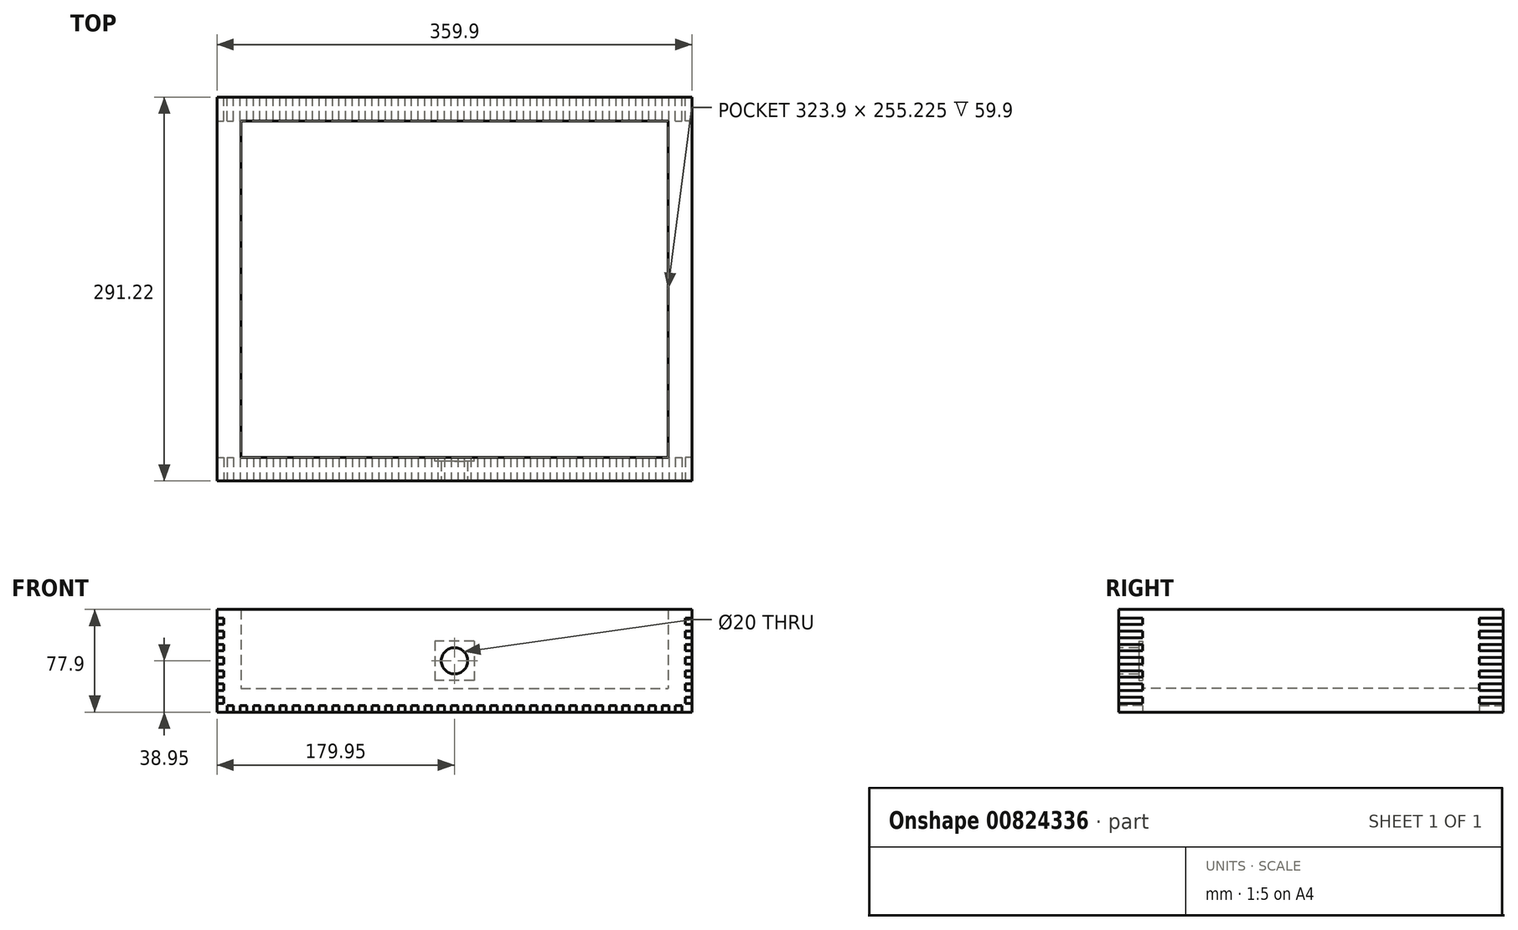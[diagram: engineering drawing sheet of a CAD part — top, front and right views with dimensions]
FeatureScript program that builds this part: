
annotation { "Feature Type Name" : "Feature", "Feature Type Description" : "" }
export const myFeature = defineFeature(function(context is Context, id is Id, definition is map)
    precondition{}
    {
        {
            var Q0;
            Q0=qCreatedBy(makeId("Top.planeOp"),FACE);
            var sketch = newSketch(context, id + "F0", { "sketchPlane" : qUnion([Q0])});
            skLineSegment(sketch, "E0.bottom", {"start": v(-179.95, 145.61) * mm, "end": v(179.95, 145.61) * mm});
            skLineSegment(sketch, "E0.top", {"start": v(-179.95, -145.61) * mm, "end": v(179.95, -145.61) * mm});
            skLineSegment(sketch, "E0.left", {"start": v(-179.95, 145.61) * mm, "end": v(-179.95, -145.61) * mm});
            skLineSegment(sketch, "E0.right", {"start": v(179.95, 145.61) * mm, "end": v(179.95, -145.61) * mm});
            skPoint(sketch, "E0.middle", {"position": v(0, 0) * mm});
            skSolve(sketch);
        }
        {
            var Q0;
            Q0 = qSketchRegion(id + "F0", true);
            extrude(context, id + "F1", {"entities" : qUnion([Q0]), "depth" : 18 * mm, "offsetDistance" : 25 * mm});
        }
        {
            var Q0;
            Q0=makeQuery(id+"F1.opExtrude","CAP_FACE",FACE,{"disambiguationData":[OSD([sQuery(id+"F0.wireOp",EDGE,"E0.bottom"),sQuery(id+"F0.wireOp",EDGE,"E0.top"),sQuery(id+"F0.wireOp",EDGE,"E0.left"),sQuery(id+"F0.wireOp",EDGE,"E0.right")])],"isStart":false});
            var sketch = newSketch(context, id + "F2", { "sketchPlane" : qUnion([Q0])});
            skLineSegment(sketch, "E1.bottom", {"start": v(-179.95, -145.61) * mm, "end": v(179.95, -145.61) * mm});
            skLineSegment(sketch, "E1.top", {"start": v(-179.95, -127.61) * mm, "end": v(179.95, -127.61) * mm});
            skLineSegment(sketch, "E1.left", {"start": v(-179.95, -145.61) * mm, "end": v(-179.95, -127.61) * mm});
            skLineSegment(sketch, "E1.right", {"start": v(179.95, -145.61) * mm, "end": v(179.95, -127.61) * mm});
            skLineSegment(sketch, "E2.MirrorCS", {"start": v(-179.95, 127.61) * mm, "end": v(179.95, 127.61) * mm});
            skLineSegment(sketch, "E3.MirrorCS", {"start": v(-179.95, 145.61) * mm, "end": v(179.95, 145.61) * mm});
            skLineSegment(sketch, "E4.MirrorCS", {"start": v(179.95, 145.61) * mm, "end": v(179.95, 127.61) * mm});
            skLineSegment(sketch, "E5.MirrorCS", {"start": v(-179.95, 145.61) * mm, "end": v(-179.95, 127.61) * mm});
            skSolve(sketch);
        }
        {
            var Q0;
            Q0 = qSketchRegion(id + "F2", true);
            extrude(context, id + "F3", {"entities" : qUnion([Q0]), "operationType" : NewBodyOperationType.ADD, "depth" : 59.9 * mm, "offsetDistance" : 25 * mm});
        }
        {
            var Q0;
            Q0=makeQuery(id+"F1.opExtrude","CAP_FACE",FACE,{"disambiguationData":[OSD([sQuery(id+"F0.wireOp",EDGE,"E0.bottom"),sQuery(id+"F0.wireOp",EDGE,"E0.top"),sQuery(id+"F0.wireOp",EDGE,"E0.left"),sQuery(id+"F0.wireOp",EDGE,"E0.right")])],"isStart":false});
            var sketch = newSketch(context, id + "F4", { "sketchPlane" : qUnion([Q0])});
            skLineSegment(sketch, "E6.bottom", {"start": v(179.95, 127.61) * mm, "end": v(161.95, 127.61) * mm});
            skLineSegment(sketch, "E6.top", {"start": v(179.95, -127.61) * mm, "end": v(161.95, -127.61) * mm});
            skLineSegment(sketch, "E6.left", {"start": v(179.95, 127.61) * mm, "end": v(179.95, -127.61) * mm});
            skLineSegment(sketch, "E6.right", {"start": v(161.95, 127.61) * mm, "end": v(161.95, -127.61) * mm});
            skLineSegment(sketch, "E7.MirrorCS", {"start": v(-179.95, 127.61) * mm, "end": v(-161.95, 127.61) * mm});
            skLineSegment(sketch, "E8.MirrorCS", {"start": v(-179.95, -127.61) * mm, "end": v(-161.95, -127.61) * mm});
            skLineSegment(sketch, "E9.MirrorCS", {"start": v(-179.95, 127.61) * mm, "end": v(-179.95, -127.61) * mm});
            skLineSegment(sketch, "E10.MirrorCS", {"start": v(-161.95, 127.61) * mm, "end": v(-161.95, -127.61) * mm});
            skSolve(sketch);
        }
        {
            var Q0;
            Q0 = qSketchRegion(id + "F4", true);
            extrude(context, id + "F5", {"entities" : qUnion([Q0]), "operationType" : NewBodyOperationType.ADD, "depth" : 59.9 * mm, "offsetDistance" : 25 * mm});
        }
        {
            var Q0;
            Q0=makeQuery(id+"F3.boolean.opBoolean","MERGE",FACE,{"derivedFrom":[makeQuery(id+"F1.opExtrude","SWEPT_FACE",FACE,{"disambiguationData":[OSD([sQuery(id+"F0.wireOp",EDGE,"E0.top")])]}),makeQuery(id+"F3.opExtrude","SWEPT_FACE",FACE,{"disambiguationData":[OSD([sQuery(id+"F2.wireOp",EDGE,"E1.bottom")])]})]});
            var sketch = newSketch(context, id + "F6", { "sketchPlane" : qUnion([Q0])});
            skLineSegment(sketch, "E11", {"start": v(0, 0) * mm, "end": v(0, 74.36) * mm, "construction": true});
            skLineSegment(sketch, "E12", {"start": v(-179.95, 38.95) * mm, "end": v(179.95, 38.95) * mm, "construction": true});
            skLineSegment(sketch, "E13.bottom", {"start": v(-179.95, 41.45) * mm, "end": v(-174.95, 41.45) * mm});
            skLineSegment(sketch, "E13.top", {"start": v(-179.95, 36.45) * mm, "end": v(-174.95, 36.45) * mm});
            skLineSegment(sketch, "E13.left", {"start": v(-179.95, 41.45) * mm, "end": v(-179.95, 36.45) * mm});
            skLineSegment(sketch, "E13.right", {"start": v(-174.95, 41.45) * mm, "end": v(-174.95, 36.45) * mm});
            skPoint(sketch, "E13.middle", {"position": v(-177.45, 38.95) * mm});
            skLineSegment(sketch, "E14.0.1.0", {"start": v(-179.95, 51.45) * mm, "end": v(-179.95, 46.45) * mm});
            skLineSegment(sketch, "E14.0.1.1", {"start": v(-174.95, 51.45) * mm, "end": v(-174.95, 46.45) * mm});
            skLineSegment(sketch, "E14.0.1.2", {"start": v(-179.95, 51.45) * mm, "end": v(-174.95, 51.45) * mm});
            skPoint(sketch, "E14.0.1.3", {"position": v(-177.45, 48.95) * mm});
            skLineSegment(sketch, "E14.0.1.4", {"start": v(-179.95, 46.45) * mm, "end": v(-174.95, 46.45) * mm});
            skLineSegment(sketch, "E14.0.2.0", {"start": v(-179.95, 61.45) * mm, "end": v(-179.95, 56.45) * mm});
            skLineSegment(sketch, "E14.0.2.1", {"start": v(-174.95, 61.45) * mm, "end": v(-174.95, 56.45) * mm});
            skLineSegment(sketch, "E14.0.2.2", {"start": v(-179.95, 61.45) * mm, "end": v(-174.95, 61.45) * mm});
            skPoint(sketch, "E14.0.2.3", {"position": v(-177.45, 58.95) * mm});
            skLineSegment(sketch, "E14.0.2.4", {"start": v(-179.95, 56.45) * mm, "end": v(-174.95, 56.45) * mm});
            skLineSegment(sketch, "E14.0.3.0", {"start": v(-179.95, 71.45) * mm, "end": v(-179.95, 66.45) * mm});
            skLineSegment(sketch, "E14.0.3.1", {"start": v(-174.95, 71.45) * mm, "end": v(-174.95, 66.45) * mm});
            skLineSegment(sketch, "E14.0.3.2", {"start": v(-179.95, 71.45) * mm, "end": v(-174.95, 71.45) * mm});
            skPoint(sketch, "E14.0.3.3", {"position": v(-177.45, 68.95) * mm});
            skLineSegment(sketch, "E14.0.3.4", {"start": v(-179.95, 66.45) * mm, "end": v(-174.95, 66.45) * mm});
            skLineSegment(sketch, "E14.direction1", {"start": v(-179.95, 36.45) * mm, "end": v(-154.95, 36.45) * mm, "construction": true});
            skLineSegment(sketch, "E14.direction2", {"start": v(-179.95, 36.45) * mm, "end": v(-179.95, 46.45) * mm, "construction": true});
            skLineSegment(sketch, "E15.MirrorCS", {"start": v(-179.95, 36.45) * mm, "end": v(-179.95, 41.45) * mm});
            skLineSegment(sketch, "E16.MirrorCS", {"start": v(-179.95, 21.45) * mm, "end": v(-174.95, 21.45) * mm});
            skPoint(sketch, "E17.MirrorP", {"position": v(-177.45, 28.95) * mm});
            skLineSegment(sketch, "E18.MirrorCS", {"start": v(-179.95, 6.45) * mm, "end": v(-174.95, 6.45) * mm});
            skLineSegment(sketch, "E19.MirrorCS", {"start": v(-174.95, 6.45) * mm, "end": v(-174.95, 11.45) * mm});
            skLineSegment(sketch, "E20.MirrorCS", {"start": v(-174.95, 16.45) * mm, "end": v(-174.95, 21.45) * mm});
            skLineSegment(sketch, "E21.MirrorCS", {"start": v(-174.95, 36.45) * mm, "end": v(-174.95, 41.45) * mm});
            skPoint(sketch, "E22.MirrorP", {"position": v(-177.45, 8.95) * mm});
            skLineSegment(sketch, "E23.MirrorCS", {"start": v(-179.95, 16.45) * mm, "end": v(-179.95, 21.45) * mm});
            skPoint(sketch, "E24.MirrorP", {"position": v(-177.45, 18.95) * mm});
            skLineSegment(sketch, "E25.MirrorCS", {"start": v(-179.95, 11.45) * mm, "end": v(-174.95, 11.45) * mm});
            skLineSegment(sketch, "E26.MirrorCS", {"start": v(-174.95, 26.45) * mm, "end": v(-174.95, 31.45) * mm});
            skLineSegment(sketch, "E27.MirrorCS", {"start": v(-179.95, 26.45) * mm, "end": v(-174.95, 26.45) * mm});
            skLineSegment(sketch, "E28.MirrorCS", {"start": v(-179.95, 6.45) * mm, "end": v(-179.95, 11.45) * mm});
            skLineSegment(sketch, "E29.MirrorCS", {"start": v(-179.95, 41.45) * mm, "end": v(-179.95, 31.45) * mm, "construction": true});
            skLineSegment(sketch, "E30.MirrorCS", {"start": v(-179.95, 31.45) * mm, "end": v(-174.95, 31.45) * mm});
            skLineSegment(sketch, "E31.MirrorCS", {"start": v(-179.95, 16.45) * mm, "end": v(-174.95, 16.45) * mm});
            skLineSegment(sketch, "E32.MirrorCS", {"start": v(-179.95, 26.45) * mm, "end": v(-179.95, 31.45) * mm});
            skLineSegment(sketch, "E33.MirrorCS", {"start": v(179.95, 41.45) * mm, "end": v(179.95, 36.45) * mm});
            skLineSegment(sketch, "E34.MirrorCS", {"start": v(179.95, 36.45) * mm, "end": v(179.95, 41.45) * mm});
            skPoint(sketch, "E35.MirrorP", {"position": v(177.45, 28.95) * mm});
            skLineSegment(sketch, "E36.MirrorCS", {"start": v(179.95, 31.45) * mm, "end": v(174.95, 31.45) * mm});
            skLineSegment(sketch, "E37.MirrorCS", {"start": v(179.95, 26.45) * mm, "end": v(179.95, 31.45) * mm});
            skPoint(sketch, "E38.MirrorP", {"position": v(177.45, 38.95) * mm});
            skLineSegment(sketch, "E39.MirrorCS", {"start": v(174.95, 26.45) * mm, "end": v(174.95, 31.45) * mm});
            skLineSegment(sketch, "E40.MirrorCS", {"start": v(179.95, 36.45) * mm, "end": v(174.95, 36.45) * mm});
            skLineSegment(sketch, "E41.MirrorCS", {"start": v(174.95, 41.45) * mm, "end": v(174.95, 36.45) * mm});
            skLineSegment(sketch, "E42.MirrorCS", {"start": v(179.95, 41.45) * mm, "end": v(174.95, 41.45) * mm});
            skLineSegment(sketch, "E43.MirrorCS", {"start": v(179.95, 26.45) * mm, "end": v(174.95, 26.45) * mm});
            skLineSegment(sketch, "E44.MirrorCS", {"start": v(179.95, 16.45) * mm, "end": v(179.95, 21.45) * mm});
            skLineSegment(sketch, "E45.MirrorCS", {"start": v(179.95, 66.45) * mm, "end": v(174.95, 66.45) * mm});
            skLineSegment(sketch, "E46.MirrorCS", {"start": v(174.95, 61.45) * mm, "end": v(174.95, 56.45) * mm});
            skPoint(sketch, "E47.MirrorP", {"position": v(177.45, 8.95) * mm});
            skPoint(sketch, "E48.MirrorP", {"position": v(177.45, 58.95) * mm});
            skLineSegment(sketch, "E49.MirrorCS", {"start": v(174.95, 51.45) * mm, "end": v(174.95, 46.45) * mm});
            skLineSegment(sketch, "E50.MirrorCS", {"start": v(179.95, 61.45) * mm, "end": v(179.95, 56.45) * mm});
            skLineSegment(sketch, "E51.MirrorCS", {"start": v(179.95, 61.45) * mm, "end": v(174.95, 61.45) * mm});
            skLineSegment(sketch, "E52.MirrorCS", {"start": v(179.95, 41.45) * mm, "end": v(179.95, 31.45) * mm, "construction": true});
            skLineSegment(sketch, "E53.MirrorCS", {"start": v(179.95, 36.45) * mm, "end": v(179.95, 46.45) * mm, "construction": true});
            skPoint(sketch, "E54.MirrorP", {"position": v(177.45, 48.95) * mm});
            skPoint(sketch, "E55.MirrorP", {"position": v(177.45, 68.95) * mm});
            skLineSegment(sketch, "E56.MirrorCS", {"start": v(179.95, 51.45) * mm, "end": v(174.95, 51.45) * mm});
            skLineSegment(sketch, "E57.MirrorCS", {"start": v(179.95, 71.45) * mm, "end": v(174.95, 71.45) * mm});
            skLineSegment(sketch, "E58.MirrorCS", {"start": v(179.95, 16.45) * mm, "end": v(174.95, 16.45) * mm});
            skLineSegment(sketch, "E59.MirrorCS", {"start": v(179.95, 46.45) * mm, "end": v(174.95, 46.45) * mm});
            skPoint(sketch, "E60.MirrorP", {"position": v(177.45, 18.95) * mm});
            skLineSegment(sketch, "E61.MirrorCS", {"start": v(174.95, 6.45) * mm, "end": v(174.95, 11.45) * mm});
            skLineSegment(sketch, "E62.MirrorCS", {"start": v(179.95, 51.45) * mm, "end": v(179.95, 46.45) * mm});
            skLineSegment(sketch, "E63.MirrorCS", {"start": v(179.95, 21.45) * mm, "end": v(174.95, 21.45) * mm});
            skLineSegment(sketch, "E64.MirrorCS", {"start": v(179.95, 56.45) * mm, "end": v(174.95, 56.45) * mm});
            skLineSegment(sketch, "E65.MirrorCS", {"start": v(179.95, 6.45) * mm, "end": v(179.95, 11.45) * mm});
            skLineSegment(sketch, "E66.MirrorCS", {"start": v(179.95, 71.45) * mm, "end": v(179.95, 66.45) * mm});
            skLineSegment(sketch, "E67.MirrorCS", {"start": v(174.95, 36.45) * mm, "end": v(174.95, 41.45) * mm});
            skLineSegment(sketch, "E68.MirrorCS", {"start": v(174.95, 16.45) * mm, "end": v(174.95, 21.45) * mm});
            skLineSegment(sketch, "E69.MirrorCS", {"start": v(179.95, 6.45) * mm, "end": v(174.95, 6.45) * mm});
            skLineSegment(sketch, "E70.MirrorCS", {"start": v(174.95, 71.45) * mm, "end": v(174.95, 66.45) * mm});
            skLineSegment(sketch, "E71.MirrorCS", {"start": v(179.95, 11.45) * mm, "end": v(174.95, 11.45) * mm});
            skLineSegment(sketch, "E72.bottom", {"start": v(-2.5, 5) * mm, "end": v(2.5, 5) * mm});
            skLineSegment(sketch, "E72.top", {"start": v(-2.5, 0) * mm, "end": v(2.5, 0) * mm});
            skLineSegment(sketch, "E72.left", {"start": v(-2.5, 5) * mm, "end": v(-2.5, 0) * mm});
            skLineSegment(sketch, "E72.right", {"start": v(2.5, 5) * mm, "end": v(2.5, 0) * mm});
            skPoint(sketch, "E72.middle", {"position": v(0, 2.5) * mm});
            skLineSegment(sketch, "E73.1.0.0", {"start": v(7.5, 5) * mm, "end": v(7.5, 0) * mm});
            skLineSegment(sketch, "E73.1.0.1", {"start": v(7.5, 5) * mm, "end": v(12.5, 5) * mm});
            skLineSegment(sketch, "E73.1.0.2", {"start": v(12.5, 5) * mm, "end": v(12.5, 0) * mm});
            skPoint(sketch, "E73.1.0.3", {"position": v(10, 2.5) * mm});
            skLineSegment(sketch, "E73.1.0.4", {"start": v(7.5, 0) * mm, "end": v(12.5, 0) * mm});
            skLineSegment(sketch, "E73.2.0.0", {"start": v(17.5, 5) * mm, "end": v(17.5, 0) * mm});
            skLineSegment(sketch, "E73.2.0.1", {"start": v(17.5, 5) * mm, "end": v(22.5, 5) * mm});
            skLineSegment(sketch, "E73.2.0.2", {"start": v(22.5, 5) * mm, "end": v(22.5, 0) * mm});
            skPoint(sketch, "E73.2.0.3", {"position": v(20, 2.5) * mm});
            skLineSegment(sketch, "E73.2.0.4", {"start": v(17.5, 0) * mm, "end": v(22.5, 0) * mm});
            skLineSegment(sketch, "E73.3.0.0", {"start": v(27.5, 5) * mm, "end": v(27.5, 0) * mm});
            skLineSegment(sketch, "E73.3.0.1", {"start": v(27.5, 5) * mm, "end": v(32.5, 5) * mm});
            skLineSegment(sketch, "E73.3.0.2", {"start": v(32.5, 5) * mm, "end": v(32.5, 0) * mm});
            skPoint(sketch, "E73.3.0.3", {"position": v(30, 2.5) * mm});
            skLineSegment(sketch, "E73.3.0.4", {"start": v(27.5, 0) * mm, "end": v(32.5, 0) * mm});
            skLineSegment(sketch, "E73.4.0.0", {"start": v(37.5, 5) * mm, "end": v(37.5, 0) * mm});
            skLineSegment(sketch, "E73.4.0.1", {"start": v(37.5, 5) * mm, "end": v(42.5, 5) * mm});
            skLineSegment(sketch, "E73.4.0.2", {"start": v(42.5, 5) * mm, "end": v(42.5, 0) * mm});
            skPoint(sketch, "E73.4.0.3", {"position": v(40, 2.5) * mm});
            skLineSegment(sketch, "E73.4.0.4", {"start": v(37.5, 0) * mm, "end": v(42.5, 0) * mm});
            skLineSegment(sketch, "E73.5.0.0", {"start": v(47.5, 5) * mm, "end": v(47.5, 0) * mm});
            skLineSegment(sketch, "E73.5.0.1", {"start": v(47.5, 5) * mm, "end": v(52.5, 5) * mm});
            skLineSegment(sketch, "E73.5.0.2", {"start": v(52.5, 5) * mm, "end": v(52.5, 0) * mm});
            skPoint(sketch, "E73.5.0.3", {"position": v(50, 2.5) * mm});
            skLineSegment(sketch, "E73.5.0.4", {"start": v(47.5, 0) * mm, "end": v(52.5, 0) * mm});
            skLineSegment(sketch, "E73.6.0.0", {"start": v(57.5, 5) * mm, "end": v(57.5, 0) * mm});
            skLineSegment(sketch, "E73.6.0.1", {"start": v(57.5, 5) * mm, "end": v(62.5, 5) * mm});
            skLineSegment(sketch, "E73.6.0.2", {"start": v(62.5, 5) * mm, "end": v(62.5, 0) * mm});
            skPoint(sketch, "E73.6.0.3", {"position": v(60, 2.5) * mm});
            skLineSegment(sketch, "E73.6.0.4", {"start": v(57.5, 0) * mm, "end": v(62.5, 0) * mm});
            skLineSegment(sketch, "E73.7.0.0", {"start": v(67.5, 5) * mm, "end": v(67.5, 0) * mm});
            skLineSegment(sketch, "E73.7.0.1", {"start": v(67.5, 5) * mm, "end": v(72.5, 5) * mm});
            skLineSegment(sketch, "E73.7.0.2", {"start": v(72.5, 5) * mm, "end": v(72.5, 0) * mm});
            skPoint(sketch, "E73.7.0.3", {"position": v(70, 2.5) * mm});
            skLineSegment(sketch, "E73.7.0.4", {"start": v(67.5, 0) * mm, "end": v(72.5, 0) * mm});
            skLineSegment(sketch, "E73.8.0.0", {"start": v(77.5, 5) * mm, "end": v(77.5, 0) * mm});
            skLineSegment(sketch, "E73.8.0.1", {"start": v(77.5, 5) * mm, "end": v(82.5, 5) * mm});
            skLineSegment(sketch, "E73.8.0.2", {"start": v(82.5, 5) * mm, "end": v(82.5, 0) * mm});
            skPoint(sketch, "E73.8.0.3", {"position": v(80, 2.5) * mm});
            skLineSegment(sketch, "E73.8.0.4", {"start": v(77.5, 0) * mm, "end": v(82.5, 0) * mm});
            skLineSegment(sketch, "E73.9.0.0", {"start": v(87.5, 5) * mm, "end": v(87.5, 0) * mm});
            skLineSegment(sketch, "E73.9.0.1", {"start": v(87.5, 5) * mm, "end": v(92.5, 5) * mm});
            skLineSegment(sketch, "E73.9.0.2", {"start": v(92.5, 5) * mm, "end": v(92.5, 0) * mm});
            skPoint(sketch, "E73.9.0.3", {"position": v(90, 2.5) * mm});
            skLineSegment(sketch, "E73.9.0.4", {"start": v(87.5, 0) * mm, "end": v(92.5, 0) * mm});
            skLineSegment(sketch, "E73.10.0.0", {"start": v(97.5, 5) * mm, "end": v(97.5, 0) * mm});
            skLineSegment(sketch, "E73.10.0.1", {"start": v(97.5, 5) * mm, "end": v(102.5, 5) * mm});
            skLineSegment(sketch, "E73.10.0.2", {"start": v(102.5, 5) * mm, "end": v(102.5, 0) * mm});
            skPoint(sketch, "E73.10.0.3", {"position": v(100, 2.5) * mm});
            skLineSegment(sketch, "E73.10.0.4", {"start": v(97.5, 0) * mm, "end": v(102.5, 0) * mm});
            skLineSegment(sketch, "E73.11.0.0", {"start": v(107.5, 5) * mm, "end": v(107.5, 0) * mm});
            skLineSegment(sketch, "E73.11.0.1", {"start": v(107.5, 5) * mm, "end": v(112.5, 5) * mm});
            skLineSegment(sketch, "E73.11.0.2", {"start": v(112.5, 5) * mm, "end": v(112.5, 0) * mm});
            skPoint(sketch, "E73.11.0.3", {"position": v(110, 2.5) * mm});
            skLineSegment(sketch, "E73.11.0.4", {"start": v(107.5, 0) * mm, "end": v(112.5, 0) * mm});
            skLineSegment(sketch, "E73.12.0.0", {"start": v(117.5, 5) * mm, "end": v(117.5, 0) * mm});
            skLineSegment(sketch, "E73.12.0.1", {"start": v(117.5, 5) * mm, "end": v(122.5, 5) * mm});
            skLineSegment(sketch, "E73.12.0.2", {"start": v(122.5, 5) * mm, "end": v(122.5, 0) * mm});
            skPoint(sketch, "E73.12.0.3", {"position": v(120, 2.5) * mm});
            skLineSegment(sketch, "E73.12.0.4", {"start": v(117.5, 0) * mm, "end": v(122.5, 0) * mm});
            skLineSegment(sketch, "E73.13.0.0", {"start": v(127.5, 5) * mm, "end": v(127.5, 0) * mm});
            skLineSegment(sketch, "E73.13.0.1", {"start": v(127.5, 5) * mm, "end": v(132.5, 5) * mm});
            skLineSegment(sketch, "E73.13.0.2", {"start": v(132.5, 5) * mm, "end": v(132.5, 0) * mm});
            skPoint(sketch, "E73.13.0.3", {"position": v(130, 2.5) * mm});
            skLineSegment(sketch, "E73.13.0.4", {"start": v(127.5, 0) * mm, "end": v(132.5, 0) * mm});
            skLineSegment(sketch, "E73.14.0.0", {"start": v(137.5, 5) * mm, "end": v(137.5, 0) * mm});
            skLineSegment(sketch, "E73.14.0.1", {"start": v(137.5, 5) * mm, "end": v(142.5, 5) * mm});
            skLineSegment(sketch, "E73.14.0.2", {"start": v(142.5, 5) * mm, "end": v(142.5, 0) * mm});
            skPoint(sketch, "E73.14.0.3", {"position": v(140, 2.5) * mm});
            skLineSegment(sketch, "E73.14.0.4", {"start": v(137.5, 0) * mm, "end": v(142.5, 0) * mm});
            skLineSegment(sketch, "E73.15.0.0", {"start": v(147.5, 5) * mm, "end": v(147.5, 0) * mm});
            skLineSegment(sketch, "E73.15.0.1", {"start": v(147.5, 5) * mm, "end": v(152.5, 5) * mm});
            skLineSegment(sketch, "E73.15.0.2", {"start": v(152.5, 5) * mm, "end": v(152.5, 0) * mm});
            skPoint(sketch, "E73.15.0.3", {"position": v(150, 2.5) * mm});
            skLineSegment(sketch, "E73.15.0.4", {"start": v(147.5, 0) * mm, "end": v(152.5, 0) * mm});
            skLineSegment(sketch, "E73.16.0.0", {"start": v(157.5, 5) * mm, "end": v(157.5, 0) * mm});
            skLineSegment(sketch, "E73.16.0.1", {"start": v(157.5, 5) * mm, "end": v(162.5, 5) * mm});
            skLineSegment(sketch, "E73.16.0.2", {"start": v(162.5, 5) * mm, "end": v(162.5, 0) * mm});
            skPoint(sketch, "E73.16.0.3", {"position": v(160, 2.5) * mm});
            skLineSegment(sketch, "E73.16.0.4", {"start": v(157.5, 0) * mm, "end": v(162.5, 0) * mm});
            skLineSegment(sketch, "E73.17.0.0", {"start": v(167.5, 5) * mm, "end": v(167.5, 0) * mm});
            skLineSegment(sketch, "E73.17.0.1", {"start": v(167.5, 5) * mm, "end": v(172.5, 5) * mm});
            skLineSegment(sketch, "E73.17.0.2", {"start": v(172.5, 5) * mm, "end": v(172.5, 0) * mm});
            skPoint(sketch, "E73.17.0.3", {"position": v(170, 2.5) * mm});
            skLineSegment(sketch, "E73.17.0.4", {"start": v(167.5, 0) * mm, "end": v(172.5, 0) * mm});
            skLineSegment(sketch, "E73.direction1", {"start": v(-2.5, 0) * mm, "end": v(7.5, 0) * mm, "construction": true});
            skLineSegment(sketch, "E74.MirrorCS", {"start": v(2.5, 0) * mm, "end": v(-7.5, 0) * mm, "construction": true});
            skLineSegment(sketch, "E75.MirrorCS", {"start": v(-157.5, 5) * mm, "end": v(-162.5, 5) * mm});
            skLineSegment(sketch, "E76.MirrorCS", {"start": v(-92.5, 5) * mm, "end": v(-92.5, 0) * mm});
            skLineSegment(sketch, "E77.MirrorCS", {"start": v(-132.5, 5) * mm, "end": v(-132.5, 0) * mm});
            skLineSegment(sketch, "E78.MirrorCS", {"start": v(-147.5, 5) * mm, "end": v(-152.5, 5) * mm});
            skLineSegment(sketch, "E79.MirrorCS", {"start": v(-82.5, 5) * mm, "end": v(-82.5, 0) * mm});
            skLineSegment(sketch, "E80.MirrorCS", {"start": v(-137.5, 5) * mm, "end": v(-142.5, 5) * mm});
            skLineSegment(sketch, "E81.MirrorCS", {"start": v(-87.5, 5) * mm, "end": v(-92.5, 5) * mm});
            skLineSegment(sketch, "E82.MirrorCS", {"start": v(-67.5, 5) * mm, "end": v(-67.5, 0) * mm});
            skLineSegment(sketch, "E83.MirrorCS", {"start": v(-167.5, 5) * mm, "end": v(-172.5, 5) * mm});
            skLineSegment(sketch, "E84.MirrorCS", {"start": v(-37.5, 5) * mm, "end": v(-37.5, 0) * mm});
            skLineSegment(sketch, "E85.MirrorCS", {"start": v(-87.5, 0) * mm, "end": v(-92.5, 0) * mm});
            skLineSegment(sketch, "E86.MirrorCS", {"start": v(-117.5, 5) * mm, "end": v(-122.5, 5) * mm});
            skLineSegment(sketch, "E87.MirrorCS", {"start": v(-172.5, 5) * mm, "end": v(-172.5, 0) * mm});
            skLineSegment(sketch, "E88.MirrorCS", {"start": v(-152.5, 5) * mm, "end": v(-152.5, 0) * mm});
            skLineSegment(sketch, "E89.MirrorCS", {"start": v(-67.5, 5) * mm, "end": v(-72.5, 5) * mm});
            skLineSegment(sketch, "E90.MirrorCS", {"start": v(-62.5, 5) * mm, "end": v(-62.5, 0) * mm});
            skLineSegment(sketch, "E91.MirrorCS", {"start": v(-7.5, 5) * mm, "end": v(-7.5, 0) * mm});
            skLineSegment(sketch, "E92.MirrorCS", {"start": v(-137.5, 0) * mm, "end": v(-142.5, 0) * mm});
            skLineSegment(sketch, "E93.MirrorCS", {"start": v(-122.5, 5) * mm, "end": v(-122.5, 0) * mm});
            skLineSegment(sketch, "E94.MirrorCS", {"start": v(-162.5, 5) * mm, "end": v(-162.5, 0) * mm});
            skLineSegment(sketch, "E95.MirrorCS", {"start": v(-97.5, 0) * mm, "end": v(-102.5, 0) * mm});
            skLineSegment(sketch, "E96.MirrorCS", {"start": v(-167.5, 5) * mm, "end": v(-167.5, 0) * mm});
            skLineSegment(sketch, "E97.MirrorCS", {"start": v(-107.5, 0) * mm, "end": v(-112.5, 0) * mm});
            skLineSegment(sketch, "E98.MirrorCS", {"start": v(-167.5, 0) * mm, "end": v(-172.5, 0) * mm});
            skLineSegment(sketch, "E99.MirrorCS", {"start": v(-117.5, 0) * mm, "end": v(-122.5, 0) * mm});
            skLineSegment(sketch, "E100.MirrorCS", {"start": v(-37.5, 5) * mm, "end": v(-42.5, 5) * mm});
            skLineSegment(sketch, "E101.MirrorCS", {"start": v(-127.5, 0) * mm, "end": v(-132.5, 0) * mm});
            skLineSegment(sketch, "E102.MirrorCS", {"start": v(-57.5, 5) * mm, "end": v(-62.5, 5) * mm});
            skLineSegment(sketch, "E103.MirrorCS", {"start": v(-107.5, 5) * mm, "end": v(-107.5, 0) * mm});
            skLineSegment(sketch, "E104.MirrorCS", {"start": v(-52.5, 5) * mm, "end": v(-52.5, 0) * mm});
            skLineSegment(sketch, "E105.MirrorCS", {"start": v(-37.5, 0) * mm, "end": v(-42.5, 0) * mm});
            skLineSegment(sketch, "E106.MirrorCS", {"start": v(-77.5, 5) * mm, "end": v(-77.5, 0) * mm});
            skLineSegment(sketch, "E107.MirrorCS", {"start": v(-17.5, 5) * mm, "end": v(-17.5, 0) * mm});
            skLineSegment(sketch, "E108.MirrorCS", {"start": v(-42.5, 5) * mm, "end": v(-42.5, 0) * mm});
            skLineSegment(sketch, "E109.MirrorCS", {"start": v(-127.5, 5) * mm, "end": v(-127.5, 0) * mm});
            skLineSegment(sketch, "E110.MirrorCS", {"start": v(-147.5, 0) * mm, "end": v(-152.5, 0) * mm});
            skLineSegment(sketch, "E111.MirrorCS", {"start": v(-107.5, 5) * mm, "end": v(-112.5, 5) * mm});
            skLineSegment(sketch, "E112.MirrorCS", {"start": v(-27.5, 5) * mm, "end": v(-27.5, 0) * mm});
            skLineSegment(sketch, "E113.MirrorCS", {"start": v(-17.5, 0) * mm, "end": v(-22.5, 0) * mm});
            skLineSegment(sketch, "E114.MirrorCS", {"start": v(-72.5, 5) * mm, "end": v(-72.5, 0) * mm});
            skLineSegment(sketch, "E115.MirrorCS", {"start": v(-17.5, 5) * mm, "end": v(-22.5, 5) * mm});
            skLineSegment(sketch, "E116.MirrorCS", {"start": v(-7.5, 5) * mm, "end": v(-12.5, 5) * mm});
            skLineSegment(sketch, "E117.MirrorCS", {"start": v(-97.5, 5) * mm, "end": v(-102.5, 5) * mm});
            skLineSegment(sketch, "E118.MirrorCS", {"start": v(-22.5, 5) * mm, "end": v(-22.5, 0) * mm});
            skLineSegment(sketch, "E119.MirrorCS", {"start": v(-57.5, 5) * mm, "end": v(-57.5, 0) * mm});
            skLineSegment(sketch, "E120.MirrorCS", {"start": v(-47.5, 0) * mm, "end": v(-52.5, 0) * mm});
            skLineSegment(sketch, "E121.MirrorCS", {"start": v(-12.5, 5) * mm, "end": v(-12.5, 0) * mm});
            skLineSegment(sketch, "E122.MirrorCS", {"start": v(-97.5, 5) * mm, "end": v(-97.5, 0) * mm});
            skLineSegment(sketch, "E123.MirrorCS", {"start": v(-47.5, 5) * mm, "end": v(-47.5, 0) * mm});
            skLineSegment(sketch, "E124.MirrorCS", {"start": v(-142.5, 5) * mm, "end": v(-142.5, 0) * mm});
            skLineSegment(sketch, "E125.MirrorCS", {"start": v(-87.5, 5) * mm, "end": v(-87.5, 0) * mm});
            skLineSegment(sketch, "E126.MirrorCS", {"start": v(-27.5, 0) * mm, "end": v(-32.5, 0) * mm});
            skLineSegment(sketch, "E127.MirrorCS", {"start": v(-127.5, 5) * mm, "end": v(-132.5, 5) * mm});
            skLineSegment(sketch, "E128.MirrorCS", {"start": v(-102.5, 5) * mm, "end": v(-102.5, 0) * mm});
            skLineSegment(sketch, "E129.MirrorCS", {"start": v(-137.5, 5) * mm, "end": v(-137.5, 0) * mm});
            skLineSegment(sketch, "E130.MirrorCS", {"start": v(-57.5, 0) * mm, "end": v(-62.5, 0) * mm});
            skLineSegment(sketch, "E131.MirrorCS", {"start": v(-32.5, 5) * mm, "end": v(-32.5, 0) * mm});
            skLineSegment(sketch, "E132.MirrorCS", {"start": v(-117.5, 5) * mm, "end": v(-117.5, 0) * mm});
            skLineSegment(sketch, "E133.MirrorCS", {"start": v(-157.5, 5) * mm, "end": v(-157.5, 0) * mm});
            skLineSegment(sketch, "E134.MirrorCS", {"start": v(-77.5, 0) * mm, "end": v(-82.5, 0) * mm});
            skLineSegment(sketch, "E135.MirrorCS", {"start": v(-47.5, 5) * mm, "end": v(-52.5, 5) * mm});
            skLineSegment(sketch, "E136.MirrorCS", {"start": v(-77.5, 5) * mm, "end": v(-82.5, 5) * mm});
            skLineSegment(sketch, "E137.MirrorCS", {"start": v(-67.5, 0) * mm, "end": v(-72.5, 0) * mm});
            skLineSegment(sketch, "E138.MirrorCS", {"start": v(-157.5, 0) * mm, "end": v(-162.5, 0) * mm});
            skLineSegment(sketch, "E139.MirrorCS", {"start": v(-7.5, 0) * mm, "end": v(-12.5, 0) * mm});
            skLineSegment(sketch, "E140.MirrorCS", {"start": v(-147.5, 5) * mm, "end": v(-147.5, 0) * mm});
            skLineSegment(sketch, "E141.MirrorCS", {"start": v(-27.5, 5) * mm, "end": v(-32.5, 5) * mm});
            skLineSegment(sketch, "E142.MirrorCS", {"start": v(-112.5, 5) * mm, "end": v(-112.5, 0) * mm});
            skPoint(sketch, "E143.MirrorP", {"position": v(-30, 2.5) * mm});
            skPoint(sketch, "E144.MirrorP", {"position": v(-10, 2.5) * mm});
            skPoint(sketch, "E145.MirrorP", {"position": v(-160, 2.5) * mm});
            skPoint(sketch, "E146.MirrorP", {"position": v(-70, 2.5) * mm});
            skPoint(sketch, "E147.MirrorP", {"position": v(-130, 2.5) * mm});
            skPoint(sketch, "E148.MirrorP", {"position": v(-20, 2.5) * mm});
            skPoint(sketch, "E149.MirrorP", {"position": v(-90, 2.5) * mm});
            skPoint(sketch, "E150.MirrorP", {"position": v(-120, 2.5) * mm});
            skPoint(sketch, "E151.MirrorP", {"position": v(-110, 2.5) * mm});
            skPoint(sketch, "E152.MirrorP", {"position": v(-60, 2.5) * mm});
            skPoint(sketch, "E153.MirrorP", {"position": v(-50, 2.5) * mm});
            skPoint(sketch, "E154.MirrorP", {"position": v(-80, 2.5) * mm});
            skPoint(sketch, "E155.MirrorP", {"position": v(-170, 2.5) * mm});
            skPoint(sketch, "E156.MirrorP", {"position": v(-140, 2.5) * mm});
            skPoint(sketch, "E157.MirrorP", {"position": v(-100, 2.5) * mm});
            skPoint(sketch, "E158.MirrorP", {"position": v(-150, 2.5) * mm});
            skPoint(sketch, "E159.MirrorP", {"position": v(-40, 2.5) * mm});
            skSolve(sketch);
        }
        {
            var Q0;
            Q0 = qSketchRegion(id + "F6", true);
            extrude(context, id + "F7", {"entities" : qUnion([Q0]), "operationType" : NewBodyOperationType.REMOVE, "oppositeDirection" : true, "depth" : 18 * mm, "offsetDistance" : 25 * mm});
        }
        {
            var Q0;
            Q0=makeQuery(id+"F3.boolean.opBoolean","MERGE",FACE,{"derivedFrom":[makeQuery(id+"F1.opExtrude","SWEPT_FACE",FACE,{"disambiguationData":[OSD([sQuery(id+"F0.wireOp",EDGE,"E0.bottom")])]}),makeQuery(id+"F3.opExtrude","SWEPT_FACE",FACE,{"disambiguationData":[OSD([sQuery(id+"F2.wireOp",EDGE,"E3.MirrorCS")])]})]});
            var sketch = newSketch(context, id + "F8", { "sketchPlane" : qUnion([Q0])});
            skLineSegment(sketch, "E160.bottom", {"start": v(-2.5, 5) * mm, "end": v(2.5, 5) * mm});
            skLineSegment(sketch, "E160.top", {"start": v(-2.5, 0) * mm, "end": v(2.5, 0) * mm});
            skLineSegment(sketch, "E160.left", {"start": v(-2.5, 5) * mm, "end": v(-2.5, 0) * mm});
            skLineSegment(sketch, "E160.right", {"start": v(2.5, 5) * mm, "end": v(2.5, 0) * mm});
            skPoint(sketch, "E160.middle", {"position": v(0, 2.5) * mm});
            skLineSegment(sketch, "E161.1.0.0", {"start": v(7.5, 5) * mm, "end": v(12.5, 5) * mm});
            skPoint(sketch, "E161.1.0.1", {"position": v(10, 2.5) * mm});
            skLineSegment(sketch, "E161.1.0.2", {"start": v(7.5, 5) * mm, "end": v(7.5, 0) * mm});
            skLineSegment(sketch, "E161.1.0.3", {"start": v(12.5, 5) * mm, "end": v(12.5, 0) * mm});
            skLineSegment(sketch, "E161.1.0.4", {"start": v(7.5, 0) * mm, "end": v(12.5, 0) * mm});
            skLineSegment(sketch, "E161.2.0.0", {"start": v(17.5, 5) * mm, "end": v(22.5, 5) * mm});
            skPoint(sketch, "E161.2.0.1", {"position": v(20, 2.5) * mm});
            skLineSegment(sketch, "E161.2.0.2", {"start": v(17.5, 5) * mm, "end": v(17.5, 0) * mm});
            skLineSegment(sketch, "E161.2.0.3", {"start": v(22.5, 5) * mm, "end": v(22.5, 0) * mm});
            skLineSegment(sketch, "E161.2.0.4", {"start": v(17.5, 0) * mm, "end": v(22.5, 0) * mm});
            skLineSegment(sketch, "E161.3.0.0", {"start": v(27.5, 5) * mm, "end": v(32.5, 5) * mm});
            skPoint(sketch, "E161.3.0.1", {"position": v(30, 2.5) * mm});
            skLineSegment(sketch, "E161.3.0.2", {"start": v(27.5, 5) * mm, "end": v(27.5, 0) * mm});
            skLineSegment(sketch, "E161.3.0.3", {"start": v(32.5, 5) * mm, "end": v(32.5, 0) * mm});
            skLineSegment(sketch, "E161.3.0.4", {"start": v(27.5, 0) * mm, "end": v(32.5, 0) * mm});
            skLineSegment(sketch, "E161.4.0.0", {"start": v(37.5, 5) * mm, "end": v(42.5, 5) * mm});
            skPoint(sketch, "E161.4.0.1", {"position": v(40, 2.5) * mm});
            skLineSegment(sketch, "E161.4.0.2", {"start": v(37.5, 5) * mm, "end": v(37.5, 0) * mm});
            skLineSegment(sketch, "E161.4.0.3", {"start": v(42.5, 5) * mm, "end": v(42.5, 0) * mm});
            skLineSegment(sketch, "E161.4.0.4", {"start": v(37.5, 0) * mm, "end": v(42.5, 0) * mm});
            skLineSegment(sketch, "E161.5.0.0", {"start": v(47.5, 5) * mm, "end": v(52.5, 5) * mm});
            skPoint(sketch, "E161.5.0.1", {"position": v(50, 2.5) * mm});
            skLineSegment(sketch, "E161.5.0.2", {"start": v(47.5, 5) * mm, "end": v(47.5, 0) * mm});
            skLineSegment(sketch, "E161.5.0.3", {"start": v(52.5, 5) * mm, "end": v(52.5, 0) * mm});
            skLineSegment(sketch, "E161.5.0.4", {"start": v(47.5, 0) * mm, "end": v(52.5, 0) * mm});
            skLineSegment(sketch, "E161.6.0.0", {"start": v(57.5, 5) * mm, "end": v(62.5, 5) * mm});
            skPoint(sketch, "E161.6.0.1", {"position": v(60, 2.5) * mm});
            skLineSegment(sketch, "E161.6.0.2", {"start": v(57.5, 5) * mm, "end": v(57.5, 0) * mm});
            skLineSegment(sketch, "E161.6.0.3", {"start": v(62.5, 5) * mm, "end": v(62.5, 0) * mm});
            skLineSegment(sketch, "E161.6.0.4", {"start": v(57.5, 0) * mm, "end": v(62.5, 0) * mm});
            skLineSegment(sketch, "E161.7.0.0", {"start": v(67.5, 5) * mm, "end": v(72.5, 5) * mm});
            skPoint(sketch, "E161.7.0.1", {"position": v(70, 2.5) * mm});
            skLineSegment(sketch, "E161.7.0.2", {"start": v(67.5, 5) * mm, "end": v(67.5, 0) * mm});
            skLineSegment(sketch, "E161.7.0.3", {"start": v(72.5, 5) * mm, "end": v(72.5, 0) * mm});
            skLineSegment(sketch, "E161.7.0.4", {"start": v(67.5, 0) * mm, "end": v(72.5, 0) * mm});
            skLineSegment(sketch, "E161.8.0.0", {"start": v(77.5, 5) * mm, "end": v(82.5, 5) * mm});
            skPoint(sketch, "E161.8.0.1", {"position": v(80, 2.5) * mm});
            skLineSegment(sketch, "E161.8.0.2", {"start": v(77.5, 5) * mm, "end": v(77.5, 0) * mm});
            skLineSegment(sketch, "E161.8.0.3", {"start": v(82.5, 5) * mm, "end": v(82.5, 0) * mm});
            skLineSegment(sketch, "E161.8.0.4", {"start": v(77.5, 0) * mm, "end": v(82.5, 0) * mm});
            skLineSegment(sketch, "E161.9.0.0", {"start": v(87.5, 5) * mm, "end": v(92.5, 5) * mm});
            skPoint(sketch, "E161.9.0.1", {"position": v(90, 2.5) * mm});
            skLineSegment(sketch, "E161.9.0.2", {"start": v(87.5, 5) * mm, "end": v(87.5, 0) * mm});
            skLineSegment(sketch, "E161.9.0.3", {"start": v(92.5, 5) * mm, "end": v(92.5, 0) * mm});
            skLineSegment(sketch, "E161.9.0.4", {"start": v(87.5, 0) * mm, "end": v(92.5, 0) * mm});
            skLineSegment(sketch, "E161.10.0.0", {"start": v(97.5, 5) * mm, "end": v(102.5, 5) * mm});
            skPoint(sketch, "E161.10.0.1", {"position": v(100, 2.5) * mm});
            skLineSegment(sketch, "E161.10.0.2", {"start": v(97.5, 5) * mm, "end": v(97.5, 0) * mm});
            skLineSegment(sketch, "E161.10.0.3", {"start": v(102.5, 5) * mm, "end": v(102.5, 0) * mm});
            skLineSegment(sketch, "E161.10.0.4", {"start": v(97.5, 0) * mm, "end": v(102.5, 0) * mm});
            skLineSegment(sketch, "E161.11.0.0", {"start": v(107.5, 5) * mm, "end": v(112.5, 5) * mm});
            skPoint(sketch, "E161.11.0.1", {"position": v(110, 2.5) * mm});
            skLineSegment(sketch, "E161.11.0.2", {"start": v(107.5, 5) * mm, "end": v(107.5, 0) * mm});
            skLineSegment(sketch, "E161.11.0.3", {"start": v(112.5, 5) * mm, "end": v(112.5, 0) * mm});
            skLineSegment(sketch, "E161.11.0.4", {"start": v(107.5, 0) * mm, "end": v(112.5, 0) * mm});
            skLineSegment(sketch, "E161.12.0.0", {"start": v(117.5, 5) * mm, "end": v(122.5, 5) * mm});
            skPoint(sketch, "E161.12.0.1", {"position": v(120, 2.5) * mm});
            skLineSegment(sketch, "E161.12.0.2", {"start": v(117.5, 5) * mm, "end": v(117.5, 0) * mm});
            skLineSegment(sketch, "E161.12.0.3", {"start": v(122.5, 5) * mm, "end": v(122.5, 0) * mm});
            skLineSegment(sketch, "E161.12.0.4", {"start": v(117.5, 0) * mm, "end": v(122.5, 0) * mm});
            skLineSegment(sketch, "E161.13.0.0", {"start": v(127.5, 5) * mm, "end": v(132.5, 5) * mm});
            skPoint(sketch, "E161.13.0.1", {"position": v(130, 2.5) * mm});
            skLineSegment(sketch, "E161.13.0.2", {"start": v(127.5, 5) * mm, "end": v(127.5, 0) * mm});
            skLineSegment(sketch, "E161.13.0.3", {"start": v(132.5, 5) * mm, "end": v(132.5, 0) * mm});
            skLineSegment(sketch, "E161.13.0.4", {"start": v(127.5, 0) * mm, "end": v(132.5, 0) * mm});
            skLineSegment(sketch, "E161.14.0.0", {"start": v(137.5, 5) * mm, "end": v(142.5, 5) * mm});
            skPoint(sketch, "E161.14.0.1", {"position": v(140, 2.5) * mm});
            skLineSegment(sketch, "E161.14.0.2", {"start": v(137.5, 5) * mm, "end": v(137.5, 0) * mm});
            skLineSegment(sketch, "E161.14.0.3", {"start": v(142.5, 5) * mm, "end": v(142.5, 0) * mm});
            skLineSegment(sketch, "E161.14.0.4", {"start": v(137.5, 0) * mm, "end": v(142.5, 0) * mm});
            skLineSegment(sketch, "E161.15.0.0", {"start": v(147.5, 5) * mm, "end": v(152.5, 5) * mm});
            skPoint(sketch, "E161.15.0.1", {"position": v(150, 2.5) * mm});
            skLineSegment(sketch, "E161.15.0.2", {"start": v(147.5, 5) * mm, "end": v(147.5, 0) * mm});
            skLineSegment(sketch, "E161.15.0.3", {"start": v(152.5, 5) * mm, "end": v(152.5, 0) * mm});
            skLineSegment(sketch, "E161.15.0.4", {"start": v(147.5, 0) * mm, "end": v(152.5, 0) * mm});
            skLineSegment(sketch, "E161.16.0.0", {"start": v(157.5, 5) * mm, "end": v(162.5, 5) * mm});
            skPoint(sketch, "E161.16.0.1", {"position": v(160, 2.5) * mm});
            skLineSegment(sketch, "E161.16.0.2", {"start": v(157.5, 5) * mm, "end": v(157.5, 0) * mm});
            skLineSegment(sketch, "E161.16.0.3", {"start": v(162.5, 5) * mm, "end": v(162.5, 0) * mm});
            skLineSegment(sketch, "E161.16.0.4", {"start": v(157.5, 0) * mm, "end": v(162.5, 0) * mm});
            skLineSegment(sketch, "E161.17.0.0", {"start": v(167.5, 5) * mm, "end": v(172.5, 5) * mm});
            skPoint(sketch, "E161.17.0.1", {"position": v(170, 2.5) * mm});
            skLineSegment(sketch, "E161.17.0.2", {"start": v(167.5, 5) * mm, "end": v(167.5, 0) * mm});
            skLineSegment(sketch, "E161.17.0.3", {"start": v(172.5, 5) * mm, "end": v(172.5, 0) * mm});
            skLineSegment(sketch, "E161.17.0.4", {"start": v(167.5, 0) * mm, "end": v(172.5, 0) * mm});
            skLineSegment(sketch, "E161.direction1", {"start": v(-2.5, 0) * mm, "end": v(7.5, 0) * mm, "construction": true});
            skLineSegment(sketch, "E162.MirrorCS", {"start": v(2.5, 0) * mm, "end": v(-7.5, 0) * mm, "construction": true});
            skLineSegment(sketch, "E163.MirrorCS", {"start": v(-147.5, 0) * mm, "end": v(-152.5, 0) * mm});
            skLineSegment(sketch, "E164.MirrorCS", {"start": v(-77.5, 0) * mm, "end": v(-82.5, 0) * mm});
            skLineSegment(sketch, "E165.MirrorCS", {"start": v(-7.5, 0) * mm, "end": v(-12.5, 0) * mm});
            skLineSegment(sketch, "E166.MirrorCS", {"start": v(-147.5, 5) * mm, "end": v(-152.5, 5) * mm});
            skLineSegment(sketch, "E167.MirrorCS", {"start": v(-77.5, 5) * mm, "end": v(-82.5, 5) * mm});
            skLineSegment(sketch, "E168.MirrorCS", {"start": v(-127.5, 5) * mm, "end": v(-132.5, 5) * mm});
            skLineSegment(sketch, "E169.MirrorCS", {"start": v(-7.5, 5) * mm, "end": v(-12.5, 5) * mm});
            skLineSegment(sketch, "E170.MirrorCS", {"start": v(-127.5, 0) * mm, "end": v(-132.5, 0) * mm});
            skLineSegment(sketch, "E171.MirrorCS", {"start": v(-27.5, 5) * mm, "end": v(-27.5, 0) * mm});
            skLineSegment(sketch, "E172.MirrorCS", {"start": v(-37.5, 5) * mm, "end": v(-42.5, 5) * mm});
            skLineSegment(sketch, "E173.MirrorCS", {"start": v(-107.5, 5) * mm, "end": v(-112.5, 5) * mm});
            skLineSegment(sketch, "E174.MirrorCS", {"start": v(-167.5, 5) * mm, "end": v(-167.5, 0) * mm});
            skLineSegment(sketch, "E175.MirrorCS", {"start": v(-97.5, 5) * mm, "end": v(-97.5, 0) * mm});
            skLineSegment(sketch, "E176.MirrorCS", {"start": v(-147.5, 5) * mm, "end": v(-147.5, 0) * mm});
            skLineSegment(sketch, "E177.MirrorCS", {"start": v(-167.5, 5) * mm, "end": v(-172.5, 5) * mm});
            skLineSegment(sketch, "E178.MirrorCS", {"start": v(-47.5, 5) * mm, "end": v(-47.5, 0) * mm});
            skLineSegment(sketch, "E179.MirrorCS", {"start": v(-67.5, 5) * mm, "end": v(-72.5, 5) * mm});
            skLineSegment(sketch, "E180.MirrorCS", {"start": v(-17.5, 5) * mm, "end": v(-22.5, 5) * mm});
            skLineSegment(sketch, "E181.MirrorCS", {"start": v(-152.5, 5) * mm, "end": v(-152.5, 0) * mm});
            skLineSegment(sketch, "E182.MirrorCS", {"start": v(-157.5, 5) * mm, "end": v(-162.5, 5) * mm});
            skLineSegment(sketch, "E183.MirrorCS", {"start": v(-7.5, 5) * mm, "end": v(-7.5, 0) * mm});
            skLineSegment(sketch, "E184.MirrorCS", {"start": v(-12.5, 5) * mm, "end": v(-12.5, 0) * mm});
            skLineSegment(sketch, "E185.MirrorCS", {"start": v(-62.5, 5) * mm, "end": v(-62.5, 0) * mm});
            skLineSegment(sketch, "E186.MirrorCS", {"start": v(-127.5, 5) * mm, "end": v(-127.5, 0) * mm});
            skLineSegment(sketch, "E187.MirrorCS", {"start": v(-67.5, 5) * mm, "end": v(-67.5, 0) * mm});
            skLineSegment(sketch, "E188.MirrorCS", {"start": v(-87.5, 5) * mm, "end": v(-92.5, 5) * mm});
            skLineSegment(sketch, "E189.MirrorCS", {"start": v(-47.5, 5) * mm, "end": v(-52.5, 5) * mm});
            skLineSegment(sketch, "E190.MirrorCS", {"start": v(-22.5, 5) * mm, "end": v(-22.5, 0) * mm});
            skLineSegment(sketch, "E191.MirrorCS", {"start": v(-112.5, 5) * mm, "end": v(-112.5, 0) * mm});
            skLineSegment(sketch, "E192.MirrorCS", {"start": v(-132.5, 5) * mm, "end": v(-132.5, 0) * mm});
            skLineSegment(sketch, "E193.MirrorCS", {"start": v(-97.5, 5) * mm, "end": v(-102.5, 5) * mm});
            skLineSegment(sketch, "E194.MirrorCS", {"start": v(-137.5, 5) * mm, "end": v(-142.5, 5) * mm});
            skLineSegment(sketch, "E195.MirrorCS", {"start": v(-137.5, 5) * mm, "end": v(-137.5, 0) * mm});
            skLineSegment(sketch, "E196.MirrorCS", {"start": v(-77.5, 5) * mm, "end": v(-77.5, 0) * mm});
            skLineSegment(sketch, "E197.MirrorCS", {"start": v(-42.5, 5) * mm, "end": v(-42.5, 0) * mm});
            skLineSegment(sketch, "E198.MirrorCS", {"start": v(-27.5, 5) * mm, "end": v(-32.5, 5) * mm});
            skLineSegment(sketch, "E199.MirrorCS", {"start": v(-117.5, 5) * mm, "end": v(-117.5, 0) * mm});
            skLineSegment(sketch, "E200.MirrorCS", {"start": v(-82.5, 5) * mm, "end": v(-82.5, 0) * mm});
            skLineSegment(sketch, "E201.MirrorCS", {"start": v(-162.5, 5) * mm, "end": v(-162.5, 0) * mm});
            skLineSegment(sketch, "E202.MirrorCS", {"start": v(-117.5, 5) * mm, "end": v(-122.5, 5) * mm});
            skLineSegment(sketch, "E203.MirrorCS", {"start": v(-57.5, 5) * mm, "end": v(-62.5, 5) * mm});
            skLineSegment(sketch, "E204.MirrorCS", {"start": v(-92.5, 5) * mm, "end": v(-92.5, 0) * mm});
            skLineSegment(sketch, "E205.MirrorCS", {"start": v(-142.5, 5) * mm, "end": v(-142.5, 0) * mm});
            skPoint(sketch, "E206.MirrorP", {"position": v(-120, 2.5) * mm});
            skPoint(sketch, "E207.MirrorP", {"position": v(-170, 2.5) * mm});
            skLineSegment(sketch, "E208.MirrorCS", {"start": v(-67.5, 0) * mm, "end": v(-72.5, 0) * mm});
            skPoint(sketch, "E209.MirrorP", {"position": v(-30, 2.5) * mm});
            skLineSegment(sketch, "E210.MirrorCS", {"start": v(-97.5, 0) * mm, "end": v(-102.5, 0) * mm});
            skLineSegment(sketch, "E211.MirrorCS", {"start": v(-72.5, 5) * mm, "end": v(-72.5, 0) * mm});
            skPoint(sketch, "E212.MirrorP", {"position": v(-50, 2.5) * mm});
            skLineSegment(sketch, "E213.MirrorCS", {"start": v(-102.5, 5) * mm, "end": v(-102.5, 0) * mm});
            skLineSegment(sketch, "E214.MirrorCS", {"start": v(-57.5, 0) * mm, "end": v(-62.5, 0) * mm});
            skLineSegment(sketch, "E215.MirrorCS", {"start": v(-157.5, 0) * mm, "end": v(-162.5, 0) * mm});
            skLineSegment(sketch, "E216.MirrorCS", {"start": v(-107.5, 5) * mm, "end": v(-107.5, 0) * mm});
            skLineSegment(sketch, "E217.MirrorCS", {"start": v(-37.5, 0) * mm, "end": v(-42.5, 0) * mm});
            skPoint(sketch, "E218.MirrorP", {"position": v(-40, 2.5) * mm});
            skLineSegment(sketch, "E219.MirrorCS", {"start": v(-137.5, 0) * mm, "end": v(-142.5, 0) * mm});
            skPoint(sketch, "E220.MirrorP", {"position": v(-110, 2.5) * mm});
            skLineSegment(sketch, "E221.MirrorCS", {"start": v(-32.5, 5) * mm, "end": v(-32.5, 0) * mm});
            skLineSegment(sketch, "E222.MirrorCS", {"start": v(-57.5, 5) * mm, "end": v(-57.5, 0) * mm});
            skLineSegment(sketch, "E223.MirrorCS", {"start": v(-107.5, 0) * mm, "end": v(-112.5, 0) * mm});
            skPoint(sketch, "E224.MirrorP", {"position": v(-10, 2.5) * mm});
            skLineSegment(sketch, "E225.MirrorCS", {"start": v(-117.5, 0) * mm, "end": v(-122.5, 0) * mm});
            skLineSegment(sketch, "E226.MirrorCS", {"start": v(-87.5, 5) * mm, "end": v(-87.5, 0) * mm});
            skLineSegment(sketch, "E227.MirrorCS", {"start": v(-157.5, 5) * mm, "end": v(-157.5, 0) * mm});
            skLineSegment(sketch, "E228.MirrorCS", {"start": v(-52.5, 5) * mm, "end": v(-52.5, 0) * mm});
            skLineSegment(sketch, "E229.MirrorCS", {"start": v(-17.5, 5) * mm, "end": v(-17.5, 0) * mm});
            skPoint(sketch, "E230.MirrorP", {"position": v(-80, 2.5) * mm});
            skPoint(sketch, "E231.MirrorP", {"position": v(-150, 2.5) * mm});
            skLineSegment(sketch, "E232.MirrorCS", {"start": v(-122.5, 5) * mm, "end": v(-122.5, 0) * mm});
            skPoint(sketch, "E233.MirrorP", {"position": v(-160, 2.5) * mm});
            skPoint(sketch, "E234.MirrorP", {"position": v(-20, 2.5) * mm});
            skLineSegment(sketch, "E235.MirrorCS", {"start": v(-87.5, 0) * mm, "end": v(-92.5, 0) * mm});
            skLineSegment(sketch, "E236.MirrorCS", {"start": v(-37.5, 5) * mm, "end": v(-37.5, 0) * mm});
            skPoint(sketch, "E237.MirrorP", {"position": v(-100, 2.5) * mm});
            skPoint(sketch, "E238.MirrorP", {"position": v(-140, 2.5) * mm});
            skLineSegment(sketch, "E239.MirrorCS", {"start": v(-47.5, 0) * mm, "end": v(-52.5, 0) * mm});
            skLineSegment(sketch, "E240.MirrorCS", {"start": v(-172.5, 5) * mm, "end": v(-172.5, 0) * mm});
            skPoint(sketch, "E241.MirrorP", {"position": v(-130, 2.5) * mm});
            skPoint(sketch, "E242.MirrorP", {"position": v(-60, 2.5) * mm});
            skPoint(sketch, "E243.MirrorP", {"position": v(-70, 2.5) * mm});
            skPoint(sketch, "E244.MirrorP", {"position": v(-90, 2.5) * mm});
            skLineSegment(sketch, "E245.MirrorCS", {"start": v(-17.5, 0) * mm, "end": v(-22.5, 0) * mm});
            skLineSegment(sketch, "E246.MirrorCS", {"start": v(-27.5, 0) * mm, "end": v(-32.5, 0) * mm});
            skLineSegment(sketch, "E247.MirrorCS", {"start": v(-167.5, 0) * mm, "end": v(-172.5, 0) * mm});
            skLineSegment(sketch, "E248.bottom", {"start": v(-179.95, 41.45) * mm, "end": v(-174.95, 41.45) * mm});
            skLineSegment(sketch, "E248.top", {"start": v(-179.95, 36.45) * mm, "end": v(-174.95, 36.45) * mm});
            skLineSegment(sketch, "E248.left", {"start": v(-179.95, 41.45) * mm, "end": v(-179.95, 36.45) * mm});
            skLineSegment(sketch, "E248.right", {"start": v(-174.95, 41.45) * mm, "end": v(-174.95, 36.45) * mm});
            skPoint(sketch, "E248.middle", {"position": v(-177.45, 38.95) * mm});
            skPoint(sketch, "E248.middle.positionSnap0", {"position": v(-179.95, 38.95) * mm});
            skPoint(sketch, "E248.centerSnap0", {"position": v(-179.95, 38.95) * mm});
            skPoint(sketch, "E249.0.1.0", {"position": v(-177.45, 48.95) * mm});
            skLineSegment(sketch, "E249.0.1.1", {"start": v(-174.95, 51.45) * mm, "end": v(-174.95, 46.45) * mm});
            skLineSegment(sketch, "E249.0.1.2", {"start": v(-179.95, 46.45) * mm, "end": v(-174.95, 46.45) * mm});
            skLineSegment(sketch, "E249.0.1.3", {"start": v(-179.95, 51.45) * mm, "end": v(-174.95, 51.45) * mm});
            skPoint(sketch, "E249.0.1.4", {"position": v(-179.95, 48.95) * mm});
            skLineSegment(sketch, "E249.0.1.5", {"start": v(-179.95, 51.45) * mm, "end": v(-179.95, 46.45) * mm});
            skPoint(sketch, "E249.0.1.6", {"position": v(-179.95, 48.95) * mm});
            skPoint(sketch, "E249.0.2.0", {"position": v(-177.45, 58.95) * mm});
            skLineSegment(sketch, "E249.0.2.1", {"start": v(-174.95, 61.45) * mm, "end": v(-174.95, 56.45) * mm});
            skLineSegment(sketch, "E249.0.2.2", {"start": v(-179.95, 56.45) * mm, "end": v(-174.95, 56.45) * mm});
            skLineSegment(sketch, "E249.0.2.3", {"start": v(-179.95, 61.45) * mm, "end": v(-174.95, 61.45) * mm});
            skPoint(sketch, "E249.0.2.4", {"position": v(-179.95, 58.95) * mm});
            skLineSegment(sketch, "E249.0.2.5", {"start": v(-179.95, 61.45) * mm, "end": v(-179.95, 56.45) * mm});
            skPoint(sketch, "E249.0.2.6", {"position": v(-179.95, 58.95) * mm});
            skLineSegment(sketch, "E249.direction1", {"start": v(-179.95, 36.45) * mm, "end": v(-154.95, 36.45) * mm, "construction": true});
            skLineSegment(sketch, "E249.direction2", {"start": v(-179.95, 36.45) * mm, "end": v(-179.95, 46.45) * mm, "construction": true});
            skPoint(sketch, "E250.MirrorP", {"position": v(-179.95, 18.95) * mm});
            skPoint(sketch, "E251.MirrorP", {"position": v(-179.95, 28.95) * mm});
            skLineSegment(sketch, "E252.MirrorCS", {"start": v(-179.95, 26.45) * mm, "end": v(-179.95, 31.45) * mm});
            skPoint(sketch, "E253.MirrorP", {"position": v(-177.45, 18.95) * mm});
            skLineSegment(sketch, "E254.MirrorCS", {"start": v(-179.95, 26.45) * mm, "end": v(-174.95, 26.45) * mm});
            skPoint(sketch, "E255.MirrorP", {"position": v(-177.45, 28.95) * mm});
            skLineSegment(sketch, "E256.MirrorCS", {"start": v(-174.95, 26.45) * mm, "end": v(-174.95, 31.45) * mm});
            skLineSegment(sketch, "E257.MirrorCS", {"start": v(-179.95, 31.45) * mm, "end": v(-174.95, 31.45) * mm});
            skLineSegment(sketch, "E258.MirrorCS", {"start": v(-174.95, 16.45) * mm, "end": v(-174.95, 21.45) * mm});
            skLineSegment(sketch, "E259.MirrorCS", {"start": v(-179.95, 16.45) * mm, "end": v(-174.95, 16.45) * mm});
            skLineSegment(sketch, "E260.MirrorCS", {"start": v(-179.95, 16.45) * mm, "end": v(-179.95, 21.45) * mm});
            skLineSegment(sketch, "E261.MirrorCS", {"start": v(-179.95, 21.45) * mm, "end": v(-174.95, 21.45) * mm});
            skPoint(sketch, "E262.0.0.3", {"position": v(-177.45, 68.95) * mm});
            skLineSegment(sketch, "E262.1.0.3", {"start": v(-174.95, 71.45) * mm, "end": v(-174.95, 66.45) * mm});
            skLineSegment(sketch, "E262.4.0.3", {"start": v(-179.95, 66.45) * mm, "end": v(-174.95, 66.45) * mm});
            skLineSegment(sketch, "E262.7.0.3", {"start": v(-179.95, 71.45) * mm, "end": v(-174.95, 71.45) * mm});
            skPoint(sketch, "E262.10.0.3", {"position": v(-179.95, 68.95) * mm});
            skLineSegment(sketch, "E262.11.0.3", {"start": v(-179.95, 71.45) * mm, "end": v(-179.95, 66.45) * mm});
            skPoint(sketch, "E262.14.0.3", {"position": v(-179.95, 68.95) * mm});
            skPoint(sketch, "E263.MirrorP", {"position": v(-179.95, 8.95) * mm});
            skLineSegment(sketch, "E264.MirrorCS", {"start": v(-174.95, 6.45) * mm, "end": v(-174.95, 11.45) * mm});
            skLineSegment(sketch, "E265.MirrorCS", {"start": v(-179.95, 6.45) * mm, "end": v(-174.95, 6.45) * mm});
            skLineSegment(sketch, "E266.MirrorCS", {"start": v(-179.95, 6.45) * mm, "end": v(-179.95, 11.45) * mm});
            skLineSegment(sketch, "E267.MirrorCS", {"start": v(-179.95, 11.45) * mm, "end": v(-174.95, 11.45) * mm});
            skPoint(sketch, "E268.MirrorP", {"position": v(-177.45, 8.95) * mm});
            skLineSegment(sketch, "E269.MirrorCS", {"start": v(179.95, 21.45) * mm, "end": v(174.95, 21.45) * mm});
            skLineSegment(sketch, "E270.MirrorCS", {"start": v(179.95, 36.45) * mm, "end": v(174.95, 36.45) * mm});
            skLineSegment(sketch, "E271.MirrorCS", {"start": v(179.95, 41.45) * mm, "end": v(179.95, 36.45) * mm});
            skLineSegment(sketch, "E272.MirrorCS", {"start": v(179.95, 16.45) * mm, "end": v(179.95, 21.45) * mm});
            skLineSegment(sketch, "E273.MirrorCS", {"start": v(179.95, 36.45) * mm, "end": v(179.95, 46.45) * mm, "construction": true});
            skLineSegment(sketch, "E274.MirrorCS", {"start": v(179.95, 61.45) * mm, "end": v(179.95, 56.45) * mm});
            skLineSegment(sketch, "E275.MirrorCS", {"start": v(179.95, 46.45) * mm, "end": v(174.95, 46.45) * mm});
            skLineSegment(sketch, "E276.MirrorCS", {"start": v(179.95, 31.45) * mm, "end": v(174.95, 31.45) * mm});
            skLineSegment(sketch, "E277.MirrorCS", {"start": v(174.95, 6.45) * mm, "end": v(174.95, 11.45) * mm});
            skLineSegment(sketch, "E278.MirrorCS", {"start": v(179.95, 26.45) * mm, "end": v(179.95, 31.45) * mm});
            skLineSegment(sketch, "E279.MirrorCS", {"start": v(174.95, 16.45) * mm, "end": v(174.95, 21.45) * mm});
            skLineSegment(sketch, "E280.MirrorCS", {"start": v(179.95, 6.45) * mm, "end": v(179.95, 11.45) * mm});
            skLineSegment(sketch, "E281.MirrorCS", {"start": v(179.95, 56.45) * mm, "end": v(174.95, 56.45) * mm});
            skLineSegment(sketch, "E282.MirrorCS", {"start": v(179.95, 51.45) * mm, "end": v(174.95, 51.45) * mm});
            skLineSegment(sketch, "E283.MirrorCS", {"start": v(179.95, 41.45) * mm, "end": v(174.95, 41.45) * mm});
            skLineSegment(sketch, "E284.MirrorCS", {"start": v(179.95, 11.45) * mm, "end": v(174.95, 11.45) * mm});
            skLineSegment(sketch, "E285.MirrorCS", {"start": v(179.95, 51.45) * mm, "end": v(179.95, 46.45) * mm});
            skLineSegment(sketch, "E286.MirrorCS", {"start": v(174.95, 41.45) * mm, "end": v(174.95, 36.45) * mm});
            skLineSegment(sketch, "E287.MirrorCS", {"start": v(174.95, 51.45) * mm, "end": v(174.95, 46.45) * mm});
            skLineSegment(sketch, "E288.MirrorCS", {"start": v(179.95, 71.45) * mm, "end": v(174.95, 71.45) * mm});
            skLineSegment(sketch, "E289.MirrorCS", {"start": v(179.95, 71.45) * mm, "end": v(179.95, 66.45) * mm});
            skLineSegment(sketch, "E290.MirrorCS", {"start": v(174.95, 61.45) * mm, "end": v(174.95, 56.45) * mm});
            skLineSegment(sketch, "E291.MirrorCS", {"start": v(179.95, 26.45) * mm, "end": v(174.95, 26.45) * mm});
            skLineSegment(sketch, "E292.MirrorCS", {"start": v(179.95, 61.45) * mm, "end": v(174.95, 61.45) * mm});
            skLineSegment(sketch, "E293.MirrorCS", {"start": v(174.95, 26.45) * mm, "end": v(174.95, 31.45) * mm});
            skLineSegment(sketch, "E294.MirrorCS", {"start": v(179.95, 66.45) * mm, "end": v(174.95, 66.45) * mm});
            skLineSegment(sketch, "E295.MirrorCS", {"start": v(174.95, 71.45) * mm, "end": v(174.95, 66.45) * mm});
            skLineSegment(sketch, "E296.MirrorCS", {"start": v(179.95, 6.45) * mm, "end": v(174.95, 6.45) * mm});
            skLineSegment(sketch, "E297.MirrorCS", {"start": v(179.95, 16.45) * mm, "end": v(174.95, 16.45) * mm});
            skPoint(sketch, "E298.MirrorP", {"position": v(179.95, 38.95) * mm});
            skPoint(sketch, "E299.MirrorP", {"position": v(179.95, 48.95) * mm});
            skPoint(sketch, "E300.MirrorP", {"position": v(179.95, 18.95) * mm});
            skPoint(sketch, "E301.MirrorP", {"position": v(179.95, 28.95) * mm});
            skPoint(sketch, "E302.MirrorP", {"position": v(179.95, 68.95) * mm});
            skPoint(sketch, "E303.MirrorP", {"position": v(179.95, 8.95) * mm});
            skPoint(sketch, "E304.MirrorP", {"position": v(179.95, 58.95) * mm});
            skPoint(sketch, "E305.MirrorP", {"position": v(177.45, 58.95) * mm});
            skPoint(sketch, "E306.MirrorP", {"position": v(177.45, 18.95) * mm});
            skPoint(sketch, "E307.MirrorP", {"position": v(177.45, 8.95) * mm});
            skPoint(sketch, "E308.MirrorP", {"position": v(177.45, 38.95) * mm});
            skPoint(sketch, "E309.MirrorP", {"position": v(177.45, 28.95) * mm});
            skPoint(sketch, "E310.MirrorP", {"position": v(177.45, 68.95) * mm});
            skPoint(sketch, "E311.MirrorP", {"position": v(177.45, 48.95) * mm});
            skSolve(sketch);
        }
        {
            var Q0;
            Q0 = qSketchRegion(id + "F8", true);
            extrude(context, id + "F9", {"entities" : qUnion([Q0]), "operationType" : NewBodyOperationType.REMOVE, "oppositeDirection" : true, "depth" : 18 * mm, "offsetDistance" : 25 * mm});
        }
        {
            var Q0;
            Q0=makeQuery(id+"F6.imprint","IMPRINT",FACE,{"disambiguationData":[TD([[makeQuery(id+"F6.imprint","IMPRINT",EDGE,{"derivedFrom":sQuery(id+"F6.wireOp",EDGE,"E14.0.1.1")}),1.0]])]});
            var sketch = newSketch(context, id + "F10", { "sketchPlane" : qUnion([Q0])});
            skCircle(sketch, "E312", {"center": v(0, 38.95) * mm, "radius": 10 * mm});
            skSolve(sketch);
        }
        {
            var Q0;
            Q0 = qSketchRegion(id + "F10", true);
            extrude(context, id + "F11", {"entities" : qUnion([Q0]), "operationType" : NewBodyOperationType.REMOVE, "oppositeDirection" : true, "depth" : 18 * mm, "offsetDistance" : 25 * mm});
        }
        {
            var Q0;
            Q0=makeQuery(id+"F3.opExtrude","SWEPT_FACE",FACE,{"disambiguationData":[OSD([sQuery(id+"F2.wireOp",EDGE,"E1.top")])]});
            var sketch = newSketch(context, id + "F12", { "sketchPlane" : qUnion([Q0])});
            skLineSegment(sketch, "E313.bottom", {"start": v(-15, 53.95) * mm, "end": v(15, 53.95) * mm});
            skLineSegment(sketch, "E313.top", {"start": v(-15, 23.95) * mm, "end": v(15, 23.95) * mm});
            skLineSegment(sketch, "E313.left", {"start": v(-15, 53.95) * mm, "end": v(-15, 23.95) * mm});
            skLineSegment(sketch, "E313.right", {"start": v(15, 53.95) * mm, "end": v(15, 23.95) * mm});
            skPoint(sketch, "E313.middle", {"position": v(0, 38.95) * mm});
            skSolve(sketch);
        }
        {
            var Q0;
            Q0 = qSketchRegion(id + "F12", true);
            extrude(context, id + "F13", {"entities" : qUnion([Q0]), "operationType" : NewBodyOperationType.REMOVE, "oppositeDirection" : true, "depth" : 3 * mm, "offsetDistance" : 25 * mm});
        }
    });
